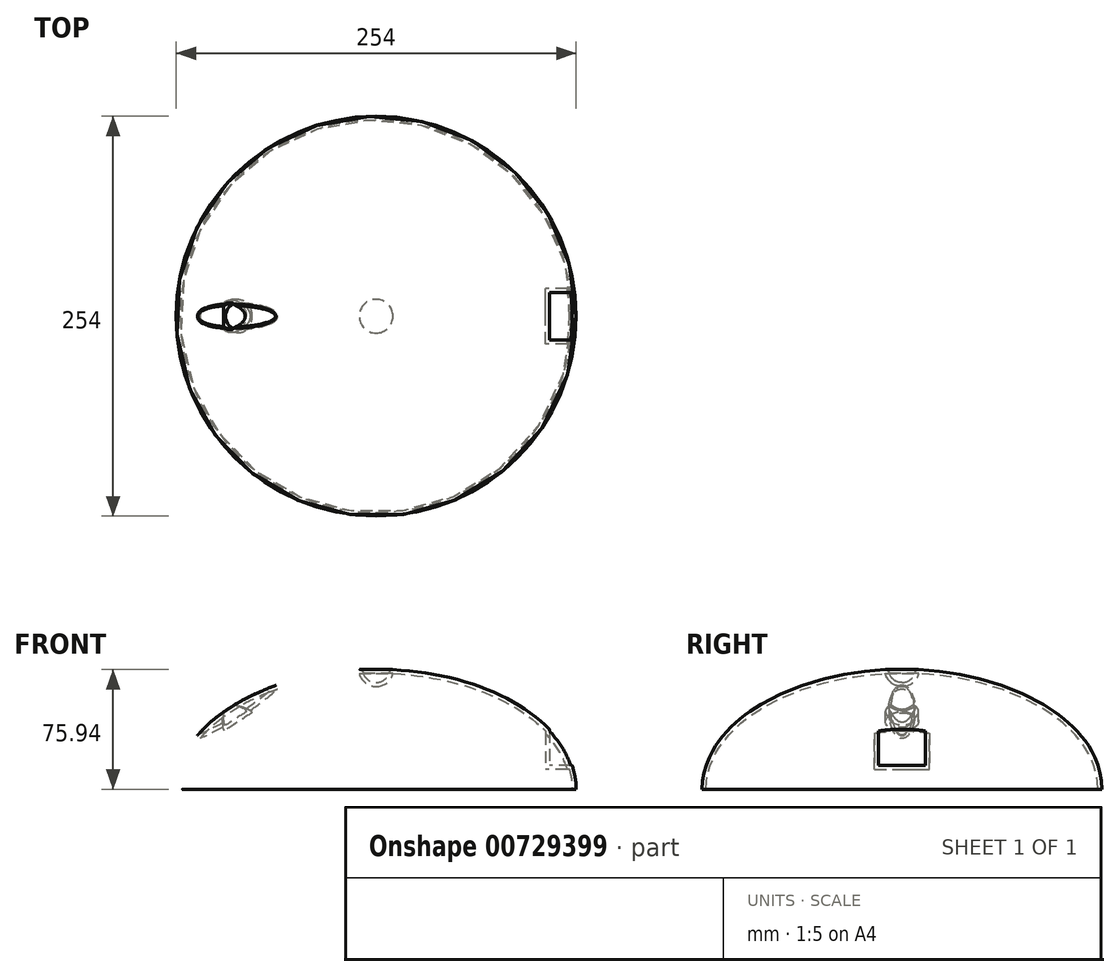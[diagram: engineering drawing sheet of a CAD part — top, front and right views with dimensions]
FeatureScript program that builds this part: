
annotation { "Feature Type Name" : "Feature", "Feature Type Description" : "" }
export const myFeature = defineFeature(function(context is Context, id is Id, definition is map)
    precondition{}
    {
        {
            var Q0;
            Q0=qCreatedBy(makeId("Front.planeOp"),FACE);
            var sketch = newSketch(context, id + "F0", { "sketchPlane" : qUnion([Q0])});
            skLineSegment(sketch, "E0", {"start": v(0, 76.2) * mm, "end": v(0, 0) * mm});
            skLineSegment(sketch, "E1", {"start": v(-127, 0) * mm, "end": v(0, 0) * mm});
            skPoint(sketch, "E2.orphan", {"position": v(-213.92, 0) * mm});
            skEllipticalArc(sketch, "E3.trimOffspring", {});
            skPoint(sketch, "E4.orphan", {"position": v(0, 240.59) * mm});
            const initialGuessF0  = {"E3.trimOffspring": [0, 0, 1, 0, 0.127, 0.0762, 1.5707963267948966, 3.141592653589793]};
            skSetInitialGuess(sketch, initialGuessF0);
            skSolve(sketch);
        }
        {
            var Q0;
            Q0=makeQuery(id+"F0.imprint","IMPRINT",FACE,{"disambiguationData":[TD([[makeQuery(id+"F0.imprint","IMPRINT",EDGE,{"derivedFrom":sQuery(id+"F0.wireOp",EDGE,"E0")}),-1.0]])]});
            var Q1;
            Q1=sQuery(id+"F0.wireOp",EDGE,"E0");
            revolve(context, id + "F1", {"surfaceOperationType" : NewSurfaceOperationType.NEW, "entities" : qUnion([Q0]), "axis" : qUnion([Q1]), "revolveType" : RevolveType.FULL});
        }
        {
            var Q0;
            Q0=qCreatedBy(makeId("Front.planeOp"),FACE);
            var sketch = newSketch(context, id + "F2", { "sketchPlane" : qUnion([Q0])});
            skLineSegment(sketch, "E5", {"start": v(-113.4, 38.65) * mm, "end": v(-25.76, 95.56) * mm});
            skLineSegment(sketch, "E6", {"start": v(-93.28, 51.71) * mm, "end": v(-83.41, 36.52) * mm});
            skSolve(sketch);
        }
        {
            var Q0;
            Q0=sQuery(id+"F2.wireOp",EDGE,"E5");
            cPlane(context, id + "F3", {"entities" : qUnion([Q0]), "cplaneType" : CPlaneType.LINE_ANGLE, "offset" : 25.4 * mm, "angle" : 90 * degree, "width" : 152.4 * mm, "height" : 152.4 * mm});
        }
        {
            var Q0;
            Q0=qCreatedBy(id+"F3.planeOp",FACE);
            var sketch = newSketch(context, id + "F4", { "sketchPlane" : qUnion([Q0])});
            skCircle(sketch, "E7", {"center": v(-50.07, 0) * mm, "radius": 8 * mm});
            skSolve(sketch);
        }
        {
            var Q0;
            Q0=qCreatedBy(id+"F3.planeOp",FACE);
            cPlane(context, id + "F5", {"entities" : qUnion([Q0]), "cplaneType" : CPlaneType.OFFSET, "offset" : 8 * mm, "oppositeDirection" : true, "width" : 152.4 * mm, "height" : 152.4 * mm});
        }
        {
            var Q0;
            Q0=makeQuery(id+"F4.imprint","IMPRINT",FACE,{"disambiguationData":[TD([[makeQuery(id+"F4.imprint","IMPRINT",EDGE,{"derivedFrom":sQuery(id+"F4.wireOp",EDGE,"E7")}),1.0]])]});
            var Q1;
            Q1=qCreatedBy(id+"F5.planeOp",FACE);
            extrude(context, id + "F6", {"entities" : qUnion([Q0]), "operationType" : NewBodyOperationType.REMOVE, "endBound" : BoundingType.UP_TO_SURFACE, "oppositeDirection" : true, "depth" : 25.4 * mm, "endBoundEntityFace" : qUnion([Q1]), "offsetDistance" : 25.4 * mm});
        }
        {
            var Q0;
            Q0=qCreatedBy(id+"F5.planeOp",FACE);
            var sketch = newSketch(context, id + "F7", { "sketchPlane" : qUnion([Q0])});
            skCircle(sketch, "E8.0", {"center": v(-50.07, 0) * mm, "radius": 8 * mm, "construction": true});
            skCircle(sketch, "E9", {"center": v(-50.07, 0) * mm, "radius": 11.67 * mm});
            skCircle(sketch, "E10", {"center": v(-50.07, 0) * mm, "radius": 13.13 * mm});
            skSolve(sketch);
        }
        {
            var Q0;
            Q0=makeQuery(id+"F1.opRevolve","SWEPT_FACE",FACE,{"disambiguationData":[OSD([sQuery(id+"F0.wireOp",EDGE,"E1")])]});
            var sketch = newSketch(context, id + "F8", { "sketchPlane" : qUnion([Q0])});
            skCircle(sketch, "E11.0", {"center": v(0, 0) * mm, "radius": 117 * mm});
            skSolve(sketch);
        }
        {
            var Q0;
            Q0=qCreatedBy(makeId("Top.planeOp"),FACE);
            var sketch = newSketch(context, id + "F9", { "sketchPlane" : qUnion([Q0])});
            skCircle(sketch, "E12", {"center": v(110, 0) * mm, "radius": 4.2 * mm});
            skSolve(sketch);
        }
        {
            var Q0;
            Q0=makeQuery(id+"F6.boolean.opBoolean","INTERSECT",EDGE,{"derivedFrom":[makeQuery(id+"F1.opRevolve","SWEPT_FACE",FACE,{"disambiguationData":[OSD([sQuery(id+"F0.wireOp",EDGE,"E3.trimOffspring")])]}),makeQuery(id+"F6.opExtrude","SWEPT_FACE",FACE,{"disambiguationData":[OSD([sQuery(id+"F4.wireOp",EDGE,"E7")])]})]});
            chamfer(context, id + "F10", {"entities" : qUnion([Q0]), "width" : 0.5 * mm, "tangentPropagation" : true});
        }
        {
            var Q0;
            Q0=qCreatedBy(makeId("Front.planeOp"),FACE);
            var sketch = newSketch(context, id + "F11", { "sketchPlane" : qUnion([Q0])});
            skArc(sketch, "E13", {"start": v(-155.58, 19.93) * mm, "mid": v(-84.5, 47.68) * mm, "end": v(-30.55, 101.65) * mm});
            skLineSegment(sketch, "E14", {"start": v(-30.55, 101.65) * mm, "end": v(-10.12, 132.96) * mm, "construction": true});
            skSolve(sketch);
        }
        {
            var Q0;
            Q0=sQuery(id+"F11.wireOp",EDGE,"E14");
            var Q1;
            Q1=sQuery(id+"F11.wireOp",VERTEX,"E14.start");
            cPlane(context, id + "F12", {"entities" : qUnion([Q0, Q1]), "cplaneType" : CPlaneType.LINE_POINT, "offset" : 25 * mm, "width" : 150 * mm, "height" : 150 * mm});
        }
        {
            var Q0;
            Q0=qCreatedBy(id+"F12.planeOp",FACE);
            var sketch = newSketch(context, id + "F13", { "sketchPlane" : qUnion([Q0])});
            skLineSegment(sketch, "E15", {"start": v(-81.48, 0) * mm, "end": v(-137.95, 0) * mm, "construction": true});
            skSolve(sketch);
        }
        {
            var Q0;
            Q0=qCreatedBy(id+"F12.planeOp",FACE);
            var sketch = newSketch(context, id + "F14", { "sketchPlane" : qUnion([Q0])});
            skArc(sketch, "E16", {"start": v(-98.05, -7.9) * mm, "mid": v(-88.73, -6.78) * mm, "end": v(-82.23, 0) * mm});
            skArc(sketch, "E17.MirrorCS", {"start": v(-98.05, 7.9) * mm, "mid": v(-88.73, 6.78) * mm, "end": v(-82.23, 0) * mm});
            skLineSegment(sketch, "E18", {"start": v(-98.05, 7.9) * mm, "end": v(-98.05, -7.9) * mm});
            skSolve(sketch);
        }
        {
            var Q0;
            Q0=makeQuery(id+"F14.imprint","IMPRINT",FACE,{"disambiguationData":[TD([[makeQuery(id+"F14.imprint","IMPRINT",EDGE,{"derivedFrom":sQuery(id+"F14.wireOp",EDGE,"E16")}),1.0]])]});
            var Q1;
            Q1=sQuery(id+"F11.wireOp",EDGE,"E13");
            sweep(context, id + "F15", {"operationType" : NewBodyOperationType.REMOVE, "profiles" : qUnion([Q0]), "path" : qUnion([Q1])});
        }
        {
            var Q0;
            {var subQ0=makeQuery(id+"F15.opSweep","SWEPT_EDGE",EDGE,{"disambiguationData":[OSD([sQuery(id+"F11.wireOp",EDGE,"E13"),sQuery(id+"F14.wireOp",EDGE,"E16"),sQuery(id+"F14.wireOp",EDGE,"E17.MirrorCS")])]});Q0=qUnion([makeQuery(id+"F15.boolean.opBoolean","COPY",EDGE,{"disambiguationData":[OD(1.0)],"derivedFrom":subQ0}),makeQuery(id+"F15.boolean.opBoolean","COPY",EDGE,{"disambiguationData":[OD(0.0)],"derivedFrom":subQ0})]);}
            fillet(context, id + "F16", {"entities" : qUnion([Q0]), "radius" : 5 * mm, "tangentPropagation" : true, "allowEdgeOverflow" : false});
        }
        {
            var Q0;
            Q0=makeQuery(id+"F15.boolean.opBoolean","INTERSECT",EDGE,{"disambiguationData":[OD(1.0)],"derivedFrom":[makeQuery(id+"F1.opRevolve","SWEPT_FACE",FACE,{"disambiguationData":[OSD([sQuery(id+"F0.wireOp",EDGE,"E3.trimOffspring")])]}),makeQuery(id+"F15.opSweep","SWEPT_FACE",FACE,{"disambiguationData":[OSD([sQuery(id+"F11.wireOp",EDGE,"E13"),sQuery(id+"F14.wireOp",EDGE,"E16")])]})]});
            var Q1;
            Q1=makeQuery(id+"F16.opFillet","BLEND_EDGE",EDGE,{"blendedFrom":[makeQuery(id+"F15.boolean.opBoolean","COPY",EDGE,{"disambiguationData":[OD(0.0)],"derivedFrom":makeQuery(id+"F15.opSweep","SWEPT_EDGE",EDGE,{"disambiguationData":[OSD([sQuery(id+"F11.wireOp",EDGE,"E13"),sQuery(id+"F14.wireOp",EDGE,"E16"),sQuery(id+"F14.wireOp",EDGE,"E17.MirrorCS")])]})}),makeQuery(id+"F1.opRevolve","SWEPT_FACE",FACE,{"disambiguationData":[OSD([sQuery(id+"F0.wireOp",EDGE,"E3.trimOffspring")])]})],"blendedInto":[makeQuery(id+"F1.opRevolve","SWEPT_FACE",FACE,{"disambiguationData":[OSD([sQuery(id+"F0.wireOp",EDGE,"E3.trimOffspring")])]})]});
            var Q2;
            {var subQ0=sQuery(id+"F14.wireOp",EDGE,"E17.MirrorCS");var subQ1=sQuery(id+"F11.wireOp",EDGE,"E13");Q2=makeQuery(id+"F16.opFillet","BLEND_EDGE",EDGE,{"blendedFrom":[makeQuery(id+"F15.boolean.opBoolean","COPY",EDGE,{"disambiguationData":[OD(0.0)],"derivedFrom":makeQuery(id+"F15.opSweep","SWEPT_EDGE",EDGE,{"disambiguationData":[OSD([subQ1,sQuery(id+"F14.wireOp",EDGE,"E16"),subQ0])]})}),makeQuery(id+"F15.boolean.opBoolean","COPY",FACE,{"disambiguationData":[OD(0.0)],"derivedFrom":makeQuery(id+"F15.opSweep","SWEPT_FACE",FACE,{"disambiguationData":[OSD([subQ1,subQ0])]})})],"blendedInto":[makeQuery(id+"F15.boolean.opBoolean","COPY",FACE,{"disambiguationData":[OD(0.0)],"derivedFrom":makeQuery(id+"F15.opSweep","SWEPT_FACE",FACE,{"disambiguationData":[OSD([subQ1,subQ0])]})})]});}
            chamfer(context, id + "F17", {"entities" : qUnion([Q0, Q1, Q2]), "width" : 1 * mm, "tangentPropagation" : true});
        }
        {
            var Q0;
            Q0=qCreatedBy(makeId("Right.planeOp"),FACE);
            var sketch = newSketch(context, id + "F18", { "sketchPlane" : qUnion([Q0])});
            skArc(sketch, "E19", {"start": v(0, 67.72) * mm, "mid": v(8.6, 76.32) * mm, "end": v(0, 84.92) * mm});
            skLineSegment(sketch, "E20", {"start": v(0, 67.72) * mm, "end": v(0, 84.92) * mm});
            skSolve(sketch);
        }
        {
            var Q0;
            Q0=makeQuery(id+"F18.imprint","IMPRINT",FACE,{"disambiguationData":[TD([[makeQuery(id+"F18.imprint","IMPRINT",EDGE,{"derivedFrom":sQuery(id+"F18.wireOp",EDGE,"E19")}),1.0]])]});
            var Q1;
            Q1=sQuery(id+"F18.wireOp",EDGE,"E20");
            revolve(context, id + "F19", {"operationType" : NewBodyOperationType.REMOVE, "surfaceOperationType" : NewSurfaceOperationType.NEW, "entities" : qUnion([Q0]), "axis" : qUnion([Q1]), "revolveType" : RevolveType.FULL, "oppositeDirection" : true});
        }
        {
            var Q0;
            Q0=makeQuery(id+"F19.boolean.opBoolean","INTERSECT",EDGE,{"derivedFrom":[makeQuery(id+"F1.opRevolve","SWEPT_FACE",FACE,{"disambiguationData":[OSD([sQuery(id+"F0.wireOp",EDGE,"E3.trimOffspring")])]}),makeQuery(id+"F19.opRevolve","SWEPT_FACE",FACE,{"disambiguationData":[OSD([sQuery(id+"F18.wireOp",EDGE,"E19")])]})]});
            fillet(context, id + "F20", {"entities" : qUnion([Q0]), "radius" : 2 * mm, "tangentPropagation" : true, "allowEdgeOverflow" : false});
        }
        {
            var Q0;
            Q0=qCreatedBy(makeId("Right.planeOp"),FACE);
            cPlane(context, id + "F21", {"entities" : qUnion([Q0]), "cplaneType" : CPlaneType.OFFSET, "offset" : 110 * mm, "width" : 150 * mm, "height" : 150 * mm});
        }
        {
            var Q0;
            Q0=qCreatedBy(id+"F21.planeOp",FACE);
            var sketch = newSketch(context, id + "F22", { "sketchPlane" : qUnion([Q0])});
            skLineSegment(sketch, "E21.bottom", {"start": v(-15, 44) * mm, "end": v(15, 44) * mm});
            skLineSegment(sketch, "E21.top", {"start": v(-15, 15) * mm, "end": v(15, 15) * mm});
            skLineSegment(sketch, "E21.left", {"start": v(-15, 44) * mm, "end": v(-15, 15) * mm});
            skLineSegment(sketch, "E21.right", {"start": v(15, 44) * mm, "end": v(15, 15) * mm});
            skPoint(sketch, "E21.middle", {"position": v(0, 29.5) * mm});
            skSolve(sketch);
        }
        {
            var Q0;
            Q0=makeQuery(id+"F22.imprint","IMPRINT",FACE,{"disambiguationData":[TD([[makeQuery(id+"F22.imprint","IMPRINT",EDGE,{"derivedFrom":sQuery(id+"F22.wireOp",EDGE,"E21.bottom")}),-1.0]])]});
            extrude(context, id + "F23", {"entities" : qUnion([Q0]), "operationType" : NewBodyOperationType.REMOVE, "endBound" : BoundingType.THROUGH_ALL, "depth" : 25 * mm, "offsetDistance" : 25 * mm});
        }
        {
            var Q0;
            Q0=makeQuery(id+"F1.opRevolve","SWEPT_FACE",FACE,{"disambiguationData":[OSD([sQuery(id+"F0.wireOp",EDGE,"E1")])]});
            shell(context, id + "F24", {"entities" : qUnion([Q0]), "thickness" : 2.5 * mm});
        }
    });
